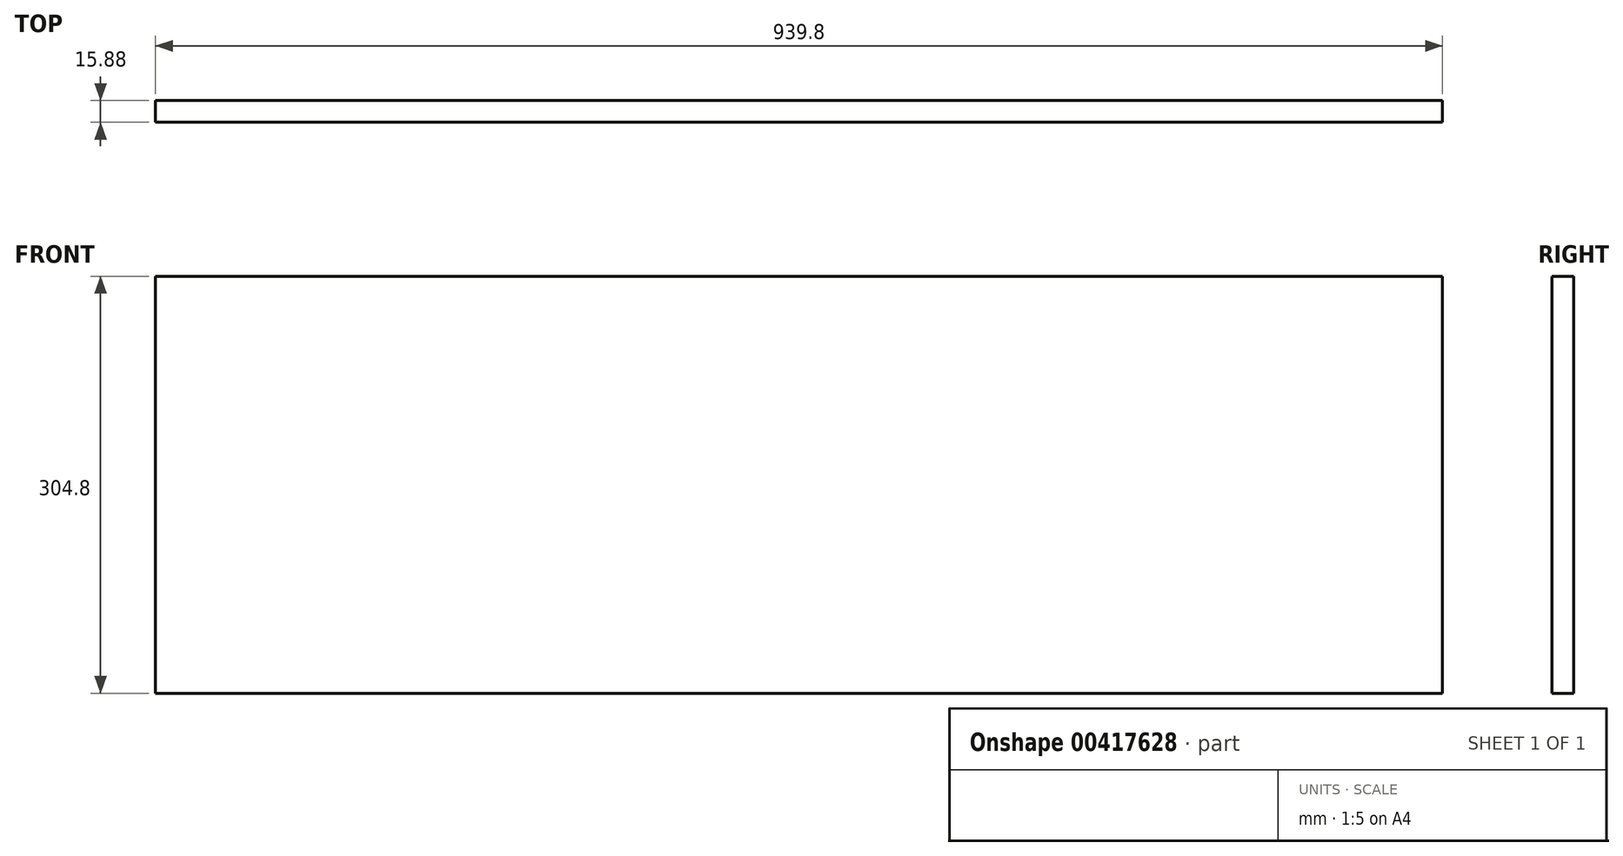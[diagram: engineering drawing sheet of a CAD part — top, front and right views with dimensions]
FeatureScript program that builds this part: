
annotation { "Feature Type Name" : "Feature", "Feature Type Description" : "" }
export const myFeature = defineFeature(function(context is Context, id is Id, definition is map)
    precondition{}
    {
        {
            var Q0;
            Q0=qCreatedBy(makeId("Front.planeOp"),FACE);
            var sketch = newSketch(context, id + "F0", { "sketchPlane" : qUnion([Q0])});
            skLineSegment(sketch, "E0.bottom", {"start": v(0, 0) * mm, "end": v(939.8, 0) * mm});
            skLineSegment(sketch, "E0.top", {"start": v(0, 304.8) * mm, "end": v(939.8, 304.8) * mm});
            skLineSegment(sketch, "E0.left", {"start": v(0, 0) * mm, "end": v(0, 304.8) * mm});
            skLineSegment(sketch, "E0.right", {"start": v(939.8, 0) * mm, "end": v(939.8, 304.8) * mm});
            skSolve(sketch);
        }
        {
            var Q0;
            Q0=makeQuery(id+"F0.imprint","IMPRINT",FACE,{"disambiguationData":[TD([[makeQuery(id+"F0.imprint","IMPRINT",EDGE,{"derivedFrom":sQuery(id+"F0.wireOp",EDGE,"E0.bottom")}),1.0]])]});
            extrude(context, id + "F1", {"entities" : qUnion([Q0]), "depth" : 15.88 * mm});
        }
    });
